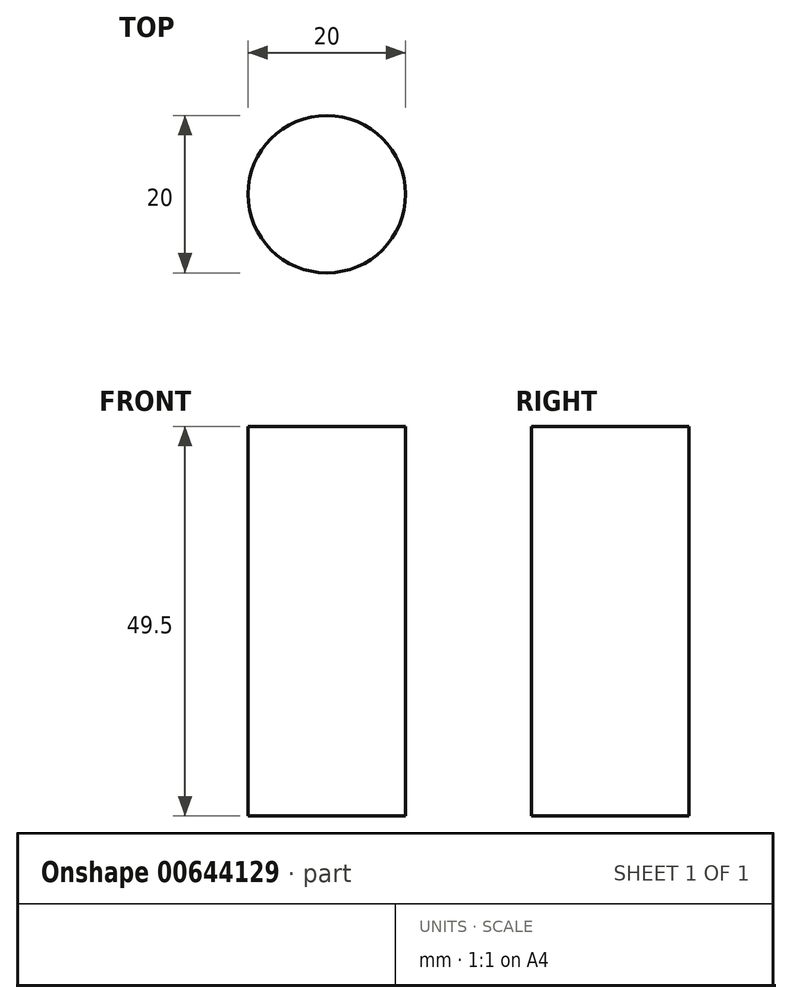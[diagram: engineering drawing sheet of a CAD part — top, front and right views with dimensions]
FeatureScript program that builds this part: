
annotation { "Feature Type Name" : "Feature", "Feature Type Description" : "" }
export const myFeature = defineFeature(function(context is Context, id is Id, definition is map)
    precondition{}
    {
        {
            var Q0;
            Q0=qCreatedBy(makeId("Top.planeOp"),FACE);
            var sketch = newSketch(context, id + "F0", { "sketchPlane" : qUnion([Q0])});
            skCircle(sketch, "E0", {"center": v(0, 0) * mm, "radius": 10 * mm});
            skSolve(sketch);
        }
        {
            var Q0;
            Q0=makeQuery(id+"F0.imprint","IMPRINT",FACE,{"disambiguationData":[TD([[makeQuery(id+"F0.imprint","IMPRINT",EDGE,{"derivedFrom":sQuery(id+"F0.wireOp",EDGE,"E0")}),1.0]])]});
            extrude(context, id + "F1", {"entities" : qUnion([Q0]), "depth" : 49.5 * mm, "offsetDistance" : 25 * mm});
        }
    });
